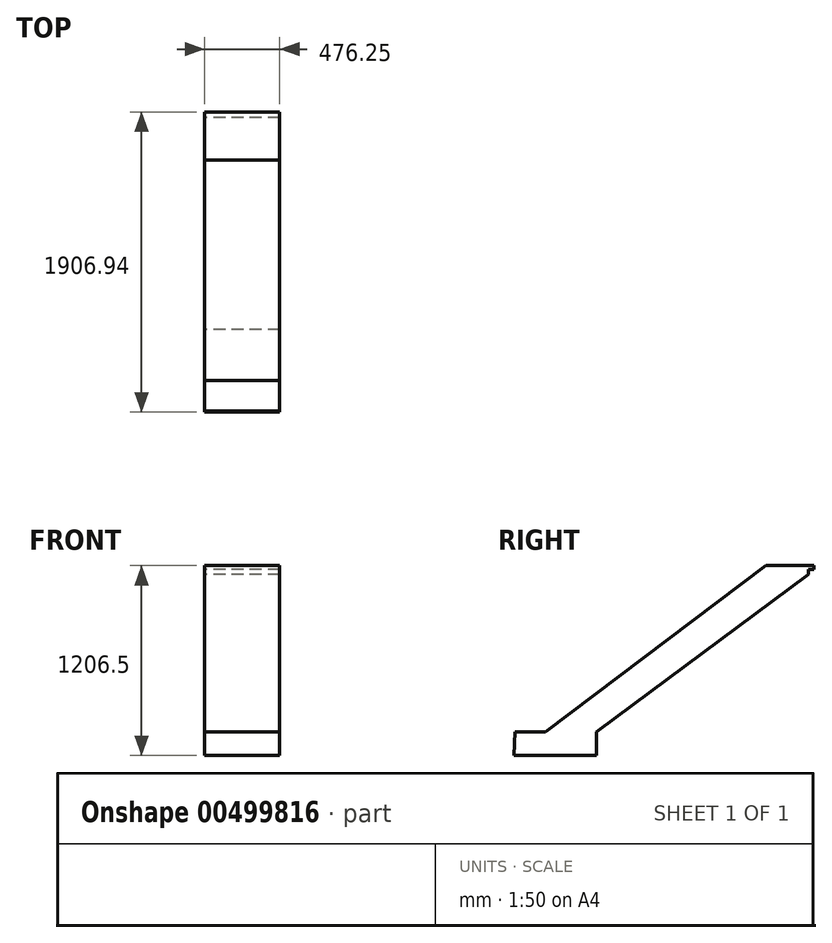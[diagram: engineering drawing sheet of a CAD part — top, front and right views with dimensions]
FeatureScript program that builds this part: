
annotation { "Feature Type Name" : "Feature", "Feature Type Description" : "" }
export const myFeature = defineFeature(function(context is Context, id is Id, definition is map)
    precondition{}
    {
        {
            var Q0;
            Q0=qCreatedBy(makeId("Right.planeOp"),FACE);
            var sketch = newSketch(context, id + "F0", { "sketchPlane" : qUnion([Q0])});
            skLineSegment(sketch, "E0", {"start": v(175.9, 45.35) * mm, "end": v(-128.9, 45.35) * mm});
            skLineSegment(sketch, "E1", {"start": v(175.9, 45.35) * mm, "end": v(175.9, 20.3) * mm});
            skLineSegment(sketch, "E2", {"start": v(-1206.37, -1161.15) * mm, "end": v(-1731.03, -1161.15) * mm});
            skLineSegment(sketch, "E3", {"start": v(-1529.98, -1009.74) * mm, "end": v(-128.9, 45.35) * mm});
            skLineSegment(sketch, "E4", {"start": v(175.9, 20.3) * mm, "end": v(139.79, 20.3) * mm});
            skLineSegment(sketch, "E5", {"start": v(139.79, 20.3) * mm, "end": v(139.79, -11.95) * mm});
            skLineSegment(sketch, "E6", {"start": v(139.79, -11.95) * mm, "end": v(-1206.37, -1009.74) * mm});
            skLineSegment(sketch, "E7", {"start": v(-1206.37, -1009.74) * mm, "end": v(-1206.37, -1161.15) * mm});
            skLineSegment(sketch, "E8", {"start": v(-1529.98, -1009.74) * mm, "end": v(-1724.44, -1009.74) * mm});
            skLineSegment(sketch, "E9", {"start": v(-1724.44, -1009.74) * mm, "end": v(-1731.03, -1161.15) * mm});
            skSolve(sketch);
        }
        {
            var Q0;
            Q0 = qSketchRegion(id + "F0", true);
            extrude(context, id + "F1", {"entities" : qUnion([Q0]), "depth" : 476.25 * mm});
        }
    });
